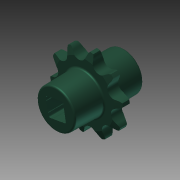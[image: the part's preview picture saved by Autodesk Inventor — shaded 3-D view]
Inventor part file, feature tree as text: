
AUTODESK INVENTOR PART (.ipt)
format: ipt  version: 2013 (Build 170138000, 138)  size: 834,048 bytes
history: native  units: mm (DEFAULTED — no unit token found)
features: imported_body x1, sketch x1, other x1, extrude x1
ambient origin geometry x8: Origin, YZ Plane, XZ Plane, XY Plane, X Axis, Y Axis, Z Axis, Center Point
bodies: Solid1 (feature_tree)
feature tree (4):
  imported_body  "Base1"
  sketch  "Sketch1"  dims[d1=2.2606mm d5=25.4mm d6=0.0mm d7=0.0mm d8=0.0mm]
  other  "Srf1"
  extrude  "ExtrusionSrf1"  Depth=25.4mm TaperAngle=0.0deg
